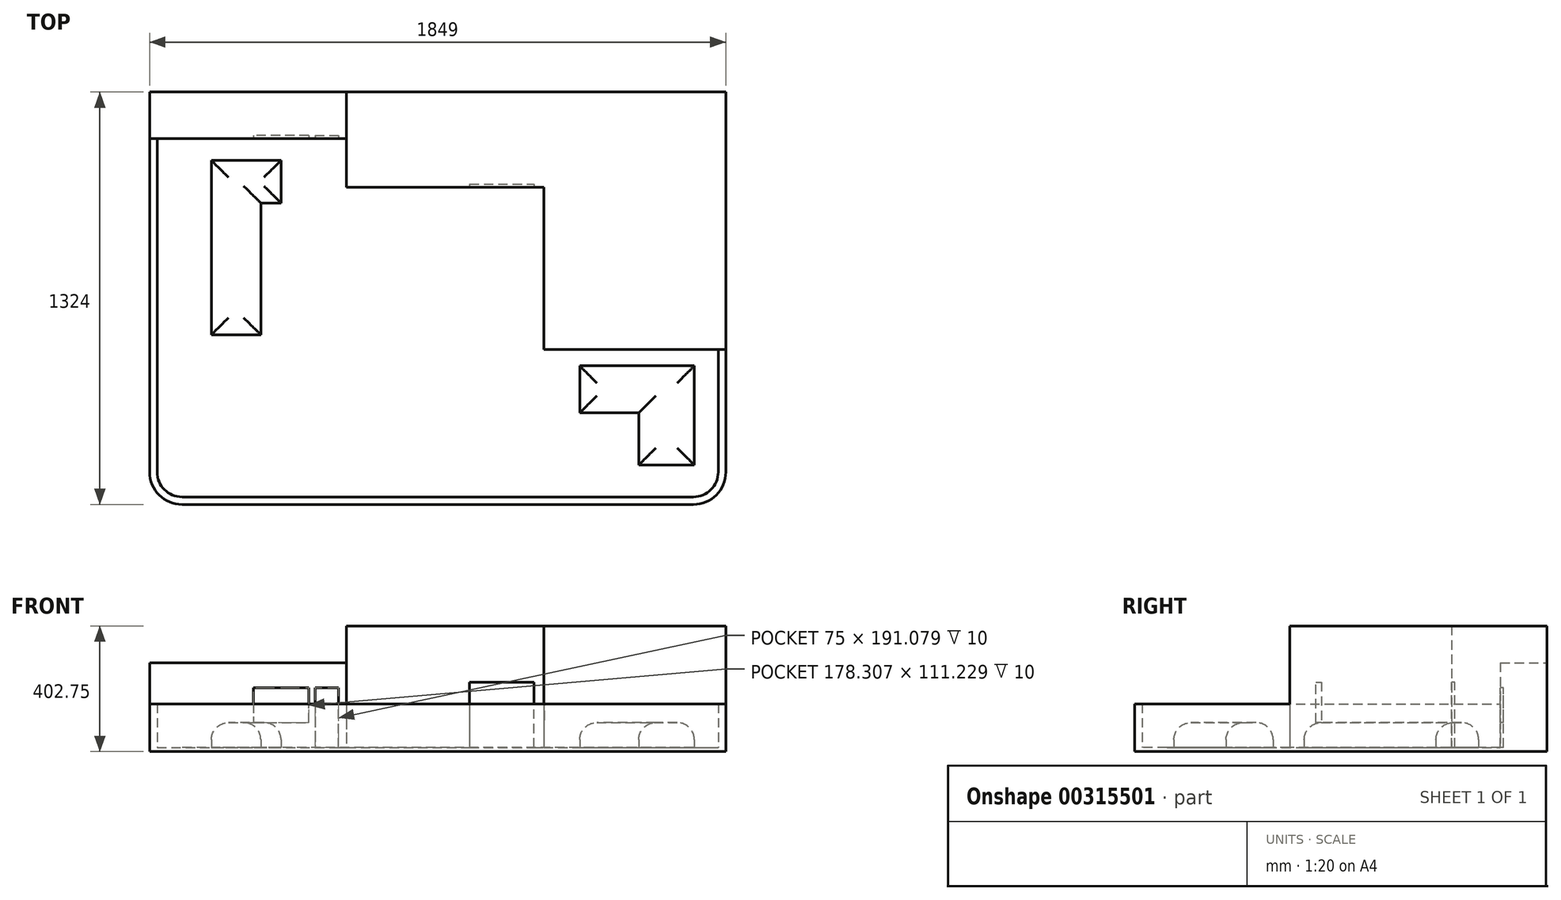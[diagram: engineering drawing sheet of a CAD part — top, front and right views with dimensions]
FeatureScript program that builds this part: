
annotation { "Feature Type Name" : "Feature", "Feature Type Description" : "" }
export const myFeature = defineFeature(function(context is Context, id is Id, definition is map)
    precondition{}
    {
        {
            var Q0;
            Q0=qCreatedBy(makeId("Top.planeOp"),FACE);
            var sketch = newSketch(context, id + "F0", { "sketchPlane" : qUnion([Q0])});
            skLineSegment(sketch, "E0", {"start": v(-3680, 5750) * mm, "end": v(-2930, 5750) * mm});
            skLineSegment(sketch, "E1", {"start": v(-2930, 5750) * mm, "end": v(-2670, 5750) * mm});
            skLineSegment(sketch, "E2", {"start": v(-2670, 5750) * mm, "end": v(-2670, 4190) * mm});
            skLineSegment(sketch, "E3", {"start": v(-2670, 4190) * mm, "end": v(1280, 4190) * mm});
            skLineSegment(sketch, "E4", {"start": v(1280, 4190) * mm, "end": v(3340, 4190) * mm});
            skLineSegment(sketch, "E5", {"start": v(3340, 4190) * mm, "end": v(3660, 4190) * mm});
            skLineSegment(sketch, "E6", {"start": v(3660, -1010) * mm, "end": v(9260, -1010) * mm});
            skLineSegment(sketch, "E7", {"start": v(9260, -1010) * mm, "end": v(9260, -4950) * mm});
            skLineSegment(sketch, "E8", {"start": v(-8750, -4950) * mm, "end": v(-8750, 5750) * mm});
            skArc(sketch, "E9", {"start": v(-8750, -4950) * mm, "mid": v(-8515.69, -5515.69) * mm, "end": v(-7950, -5750) * mm});
            skArc(sketch, "E10", {"start": v(8460, -5750) * mm, "mid": v(9025.69, -5515.69) * mm, "end": v(9260, -4950) * mm});
            skLineSegment(sketch, "E11", {"start": v(8460, -5750) * mm, "end": v(-7950, -5750) * mm});
            skLineSegment(sketch, "E12", {"start": v(3660, 4190) * mm, "end": v(3660, -1010) * mm});
            skLineSegment(sketch, "E13", {"start": v(-3680, 5750) * mm, "end": v(-8750, 5750) * mm});
            skSolve(sketch);
        }
        {
            var Q0;
            Q0=makeQuery(id+"F0.imprint","IMPRINT",FACE,{"disambiguationData":[TD([[makeQuery(id+"F0.imprint","IMPRINT",EDGE,{"derivedFrom":sQuery(id+"F0.wireOp",EDGE,"E0")}),-1.0]])]});
            extrude(context, id + "F1", {"entities" : qUnion([Q0]), "depth" : 100 * mm});
        }
        {
            var Q0;
            Q0=makeQuery(id+"F1.opExtrude","SWEPT_BODY",BODY,{"disambiguationData":[OSD([sQuery(id+"F0.wireOp",EDGE,"E0"),sQuery(id+"F0.wireOp",EDGE,"E1"),sQuery(id+"F0.wireOp",EDGE,"E2"),sQuery(id+"F0.wireOp",EDGE,"E3"),sQuery(id+"F0.wireOp",EDGE,"E4"),sQuery(id+"F0.wireOp",EDGE,"E5"),sQuery(id+"F0.wireOp",EDGE,"E6"),sQuery(id+"F0.wireOp",EDGE,"E7"),sQuery(id+"F0.wireOp",EDGE,"E8"),sQuery(id+"F0.wireOp",EDGE,"E9"),sQuery(id+"F0.wireOp",EDGE,"E10"),sQuery(id+"F0.wireOp",EDGE,"E11"),sQuery(id+"F0.wireOp",EDGE,"E12"),sQuery(id+"F0.wireOp",EDGE,"E13")])]});
            var Q1;
            Q1=qCreatedBy(makeId("Origin.pointOp"),VERTEX);
            transform(context, id + "F2", {"entities" : qUnion([Q0]), "transformType" : TransformType.SCALE_UNIFORMLY, "scale" : 1 / 10, "scalePoint" : qUnion([Q1]), "makeCopy" : false});
        }
        {
            var Q0;
            Q0=qCreatedBy(makeId("Top.planeOp"),FACE);
            var sketch = newSketch(context, id + "F3", { "sketchPlane" : qUnion([Q0])});
            skLineSegment(sketch, "E14.0", {"start": v(-899, -495) * mm, "end": v(-899, 575) * mm});
            skArc(sketch, "E15.0", {"start": v(-899, -495) * mm, "mid": v(-868.54, -568.54) * mm, "end": v(-795, -599) * mm});
            skLineSegment(sketch, "E16.0", {"start": v(846, -599) * mm, "end": v(-795, -599) * mm});
            skArc(sketch, "E17.0", {"start": v(846, -599) * mm, "mid": v(919.54, -568.54) * mm, "end": v(950, -495) * mm});
            skLineSegment(sketch, "E18.0", {"start": v(950, -101) * mm, "end": v(950, -495) * mm});
            skLineSegment(sketch, "E19.0", {"start": v(846, -575) * mm, "end": v(-795, -575) * mm});
            skArc(sketch, "E20.0", {"start": v(846, -575) * mm, "mid": v(902.57, -551.57) * mm, "end": v(926, -495) * mm});
            skLineSegment(sketch, "E21.0", {"start": v(926, -101) * mm, "end": v(926, -495) * mm});
            skLineSegment(sketch, "E22.0", {"start": v(-875, -495) * mm, "end": v(-875, 575) * mm});
            skArc(sketch, "E23.0", {"start": v(-875, -495) * mm, "mid": v(-851.57, -551.57) * mm, "end": v(-795, -575) * mm});
            skLineSegment(sketch, "E24", {"start": v(926, -101) * mm, "end": v(950, -101) * mm});
            skLineSegment(sketch, "E25", {"start": v(-875, 575) * mm, "end": v(-899, 575) * mm});
            skSolve(sketch);
        }
        {
            var Q0;
            Q0 = qSketchRegion(id + "F3", true);
            extrude(context, id + "F4", {"entities" : qUnion([Q0]), "operationType" : NewBodyOperationType.ADD, "depth" : 150 * mm});
        }
        {
            var Q0;
            Q0=qCreatedBy(makeId("Top.planeOp"),FACE);
            var sketch = newSketch(context, id + "F5", { "sketchPlane" : qUnion([Q0])});
            skLineSegment(sketch, "E26.0", {"start": v(-875, 575) * mm, "end": v(-267, 575) * mm});
            skLineSegment(sketch, "E27.0", {"start": v(-875, 575) * mm, "end": v(-899, 575) * mm});
            skLineSegment(sketch, "E28", {"start": v(-899, 575) * mm, "end": v(-899, 725) * mm});
            skLineSegment(sketch, "E29", {"start": v(-899, 725) * mm, "end": v(-267, 725) * mm});
            skLineSegment(sketch, "E30", {"start": v(-267, 725) * mm, "end": v(-267, 575) * mm});
            skSolve(sketch);
        }
        {
            var Q0;
            Q0 = qSketchRegion(id + "F5", true);
            extrude(context, id + "F6", {"entities" : qUnion([Q0]), "operationType" : NewBodyOperationType.ADD, "depth" : 282 * mm});
        }
        {
            var Q0;
            Q0=qCreatedBy(makeId("Top.planeOp"),FACE);
            var sketch = newSketch(context, id + "F7", { "sketchPlane" : qUnion([Q0])});
            skLineSegment(sketch, "E31.0", {"start": v(-267, 575) * mm, "end": v(-267, 419) * mm});
            skLineSegment(sketch, "E32.0", {"start": v(-267, 725) * mm, "end": v(-267, 575) * mm});
            skLineSegment(sketch, "E33.0", {"start": v(-267, 419) * mm, "end": v(366, 419) * mm});
            skLineSegment(sketch, "E34.0", {"start": v(366, 419) * mm, "end": v(366, -101) * mm});
            skLineSegment(sketch, "E35.0", {"start": v(366, -101) * mm, "end": v(926, -101) * mm});
            skLineSegment(sketch, "E36.0", {"start": v(926, -101) * mm, "end": v(950, -101) * mm});
            skLineSegment(sketch, "E37", {"start": v(950, -101) * mm, "end": v(950, 725) * mm});
            skLineSegment(sketch, "E38", {"start": v(950, 725) * mm, "end": v(-267, 725) * mm});
            skSolve(sketch);
        }
        {
            var Q0;
            Q0 = qSketchRegion(id + "F7", true);
            extrude(context, id + "F8", {"entities" : qUnion([Q0]), "operationType" : NewBodyOperationType.ADD, "depth" : 400 * mm});
        }
        {
            var Q0;
            Q0=makeQuery(id+"F6.opExtrude","SWEPT_FACE",FACE,{"disambiguationData":[OSD([sQuery(id+"F5.wireOp",EDGE,"E26.0"),sQuery(id+"F5.wireOp",EDGE,"E27.0")])]});
            var sketch = newSketch(context, id + "F9", { "sketchPlane" : qUnion([Q0])});
            skLineSegment(sketch, "E39.0", {"start": v(-368, 10) * mm, "end": v(-293, 10) * mm});
            skLineSegment(sketch, "E40", {"start": v(-293, 10) * mm, "end": v(-293, 201.08) * mm});
            skLineSegment(sketch, "E41", {"start": v(-293, 201.08) * mm, "end": v(-368, 201.08) * mm});
            skLineSegment(sketch, "E42", {"start": v(-368, 201.08) * mm, "end": v(-368, 10) * mm});
            skPoint(sketch, "E43.orphan", {"position": v(-267, 10) * mm});
            skPoint(sketch, "E44.orphan", {"position": v(-875, 10) * mm});
            skSolve(sketch);
        }
        {
            var Q0;
            Q0 = qSketchRegion(id + "F9", true);
            extrude(context, id + "F10", {"entities" : qUnion([Q0]), "operationType" : NewBodyOperationType.REMOVE, "oppositeDirection" : true, "depth" : 10 * mm});
        }
        {
            var Q0;
            Q0=makeQuery(id+"F6.opExtrude","SWEPT_FACE",FACE,{"disambiguationData":[OSD([sQuery(id+"F5.wireOp",EDGE,"E26.0"),sQuery(id+"F5.wireOp",EDGE,"E27.0")])]});
            var sketch = newSketch(context, id + "F11", { "sketchPlane" : qUnion([Q0])});
            skLineSegment(sketch, "E45.0", {"start": v(-368, 201.08) * mm, "end": v(-368, 10) * mm});
            skLineSegment(sketch, "E46", {"start": v(-388, 201.08) * mm, "end": v(-566.3, 201.08) * mm});
            skLineSegment(sketch, "E47", {"start": v(-566.3, 201.08) * mm, "end": v(-566.3, 89.85) * mm});
            skLineSegment(sketch, "E48", {"start": v(-566.3, 89.85) * mm, "end": v(-388, 89.85) * mm});
            skLineSegment(sketch, "E49", {"start": v(-388, 89.85) * mm, "end": v(-388, 201.08) * mm});
            skSolve(sketch);
        }
        {
            var Q0;
            Q0 = qSketchRegion(id + "F11", true);
            extrude(context, id + "F12", {"entities" : qUnion([Q0]), "operationType" : NewBodyOperationType.REMOVE, "oppositeDirection" : true, "depth" : 10 * mm});
        }
        {
            var Q0;
            Q0=makeQuery(id+"F10.boolean.opBoolean","MERGE",FACE,{"derivedFrom":[makeQuery(id+"F1.opExtrude","CAP_FACE",FACE,{"disambiguationData":[OSD([sQuery(id+"F0.wireOp",EDGE,"E0"),sQuery(id+"F0.wireOp",EDGE,"E1"),sQuery(id+"F0.wireOp",EDGE,"E2"),sQuery(id+"F0.wireOp",EDGE,"E3"),sQuery(id+"F0.wireOp",EDGE,"E4"),sQuery(id+"F0.wireOp",EDGE,"E5"),sQuery(id+"F0.wireOp",EDGE,"E6"),sQuery(id+"F0.wireOp",EDGE,"E7"),sQuery(id+"F0.wireOp",EDGE,"E8"),sQuery(id+"F0.wireOp",EDGE,"E9"),sQuery(id+"F0.wireOp",EDGE,"E10"),sQuery(id+"F0.wireOp",EDGE,"E11"),sQuery(id+"F0.wireOp",EDGE,"E12"),sQuery(id+"F0.wireOp",EDGE,"E13")])],"isStart":false}),makeQuery(id+"F10.opExtrude","SWEPT_FACE",FACE,{"disambiguationData":[OSD([sQuery(id+"F9.wireOp",EDGE,"E39.0")])]})]});
            var sketch = newSketch(context, id + "F13", { "sketchPlane" : qUnion([Q0])});
            skLineSegment(sketch, "E50.0", {"start": v(-566.3, 575) * mm, "end": v(-388, 575) * mm});
            skLineSegment(sketch, "E51", {"start": v(-477.15, 505.51) * mm, "end": v(-477.15, 368.45) * mm});
            skPoint(sketch, "E51.startSnap0", {"position": v(-477.15, 575) * mm});
            skLineSegment(sketch, "E52", {"start": v(-477.15, 368.45) * mm, "end": v(-542.33, 368.45) * mm});
            skLineSegment(sketch, "E53", {"start": v(-542.33, 368.45) * mm, "end": v(-542.33, -54.48) * mm});
            skLineSegment(sketch, "E54", {"start": v(-542.33, -54.48) * mm, "end": v(-700.93, -54.48) * mm});
            skLineSegment(sketch, "E55", {"start": v(-700.93, -54.48) * mm, "end": v(-700.93, 505.51) * mm});
            skLineSegment(sketch, "E56", {"start": v(-700.93, 505.51) * mm, "end": v(-477.15, 505.51) * mm});
            skSolve(sketch);
        }
        {
            var Q0;
            Q0 = qSketchRegion(id + "F13", true);
            var Q1;
            Q1=makeQuery(id+"F12.boolean.opBoolean","COPY",FACE,{"derivedFrom":makeQuery(id+"F12.opExtrude","SWEPT_FACE",FACE,{"disambiguationData":[OSD([sQuery(id+"F11.wireOp",EDGE,"E48")])]})});
            extrude(context, id + "F14", {"entities" : qUnion([Q0]), "operationType" : NewBodyOperationType.ADD, "endBound" : BoundingType.UP_TO_SURFACE, "endBoundEntityFace" : qUnion([Q1]), "depth" : 25 * mm});
        }
        {
            var Q0;
            Q0=makeQuery(id+"F10.boolean.opBoolean","MERGE",FACE,{"derivedFrom":[makeQuery(id+"F1.opExtrude","CAP_FACE",FACE,{"disambiguationData":[OSD([sQuery(id+"F0.wireOp",EDGE,"E0"),sQuery(id+"F0.wireOp",EDGE,"E1"),sQuery(id+"F0.wireOp",EDGE,"E2"),sQuery(id+"F0.wireOp",EDGE,"E3"),sQuery(id+"F0.wireOp",EDGE,"E4"),sQuery(id+"F0.wireOp",EDGE,"E5"),sQuery(id+"F0.wireOp",EDGE,"E6"),sQuery(id+"F0.wireOp",EDGE,"E7"),sQuery(id+"F0.wireOp",EDGE,"E8"),sQuery(id+"F0.wireOp",EDGE,"E9"),sQuery(id+"F0.wireOp",EDGE,"E10"),sQuery(id+"F0.wireOp",EDGE,"E11"),sQuery(id+"F0.wireOp",EDGE,"E12"),sQuery(id+"F0.wireOp",EDGE,"E13")])],"isStart":false}),makeQuery(id+"F10.opExtrude","SWEPT_FACE",FACE,{"disambiguationData":[OSD([sQuery(id+"F9.wireOp",EDGE,"E39.0")])]})]});
            var sketch = newSketch(context, id + "F15", { "sketchPlane" : qUnion([Q0])});
            skLineSegment(sketch, "E57", {"start": v(481.28, -153.96) * mm, "end": v(481.28, -305.16) * mm});
            skLineSegment(sketch, "E58", {"start": v(481.28, -305.16) * mm, "end": v(670.73, -305.16) * mm});
            skLineSegment(sketch, "E59", {"start": v(670.73, -305.16) * mm, "end": v(670.73, -472.75) * mm});
            skLineSegment(sketch, "E60", {"start": v(670.73, -472.75) * mm, "end": v(849.25, -472.75) * mm});
            skLineSegment(sketch, "E61", {"start": v(849.25, -472.75) * mm, "end": v(849.25, -153.96) * mm});
            skLineSegment(sketch, "E62", {"start": v(849.25, -153.96) * mm, "end": v(481.28, -153.96) * mm});
            skSolve(sketch);
        }
        {
            var Q0;
            Q0 = qSketchRegion(id + "F15", true);
            var Q1;
            Q1=makeQuery(id+"F14.opExtrude","CAP_FACE",FACE,{"disambiguationData":[OSD([sQuery(id+"F13.wireOp",EDGE,"E51"),sQuery(id+"F13.wireOp",EDGE,"E52"),sQuery(id+"F13.wireOp",EDGE,"E53"),sQuery(id+"F13.wireOp",EDGE,"E54"),sQuery(id+"F13.wireOp",EDGE,"E55"),sQuery(id+"F13.wireOp",EDGE,"E56")])],"isStart":false});
            extrude(context, id + "F16", {"entities" : qUnion([Q0]), "operationType" : NewBodyOperationType.ADD, "endBound" : BoundingType.UP_TO_SURFACE, "endBoundEntityFace" : qUnion([Q1]), "depth" : 25 * mm});
        }
        {
            var Q0;
            Q0=makeQuery(id+"F8.opExtrude","SWEPT_FACE",FACE,{"disambiguationData":[OSD([sQuery(id+"F7.wireOp",EDGE,"E33.0")])]});
            var sketch = newSketch(context, id + "F17", { "sketchPlane" : qUnion([Q0])});
            skLineSegment(sketch, "E63.0", {"start": v(-267, 10) * mm, "end": v(366, 10) * mm});
            skLineSegment(sketch, "E64", {"start": v(334, 10) * mm, "end": v(334, 220) * mm});
            skLineSegment(sketch, "E65", {"start": v(334, 220) * mm, "end": v(128, 220) * mm});
            skLineSegment(sketch, "E66", {"start": v(128, 220) * mm, "end": v(128, 10) * mm});
            skSolve(sketch);
        }
        {
            var Q0;
            Q0 = qSketchRegion(id + "F17", true);
            extrude(context, id + "F18", {"entities" : qUnion([Q0]), "operationType" : NewBodyOperationType.REMOVE, "oppositeDirection" : true, "depth" : 10 * mm});
        }
        {
            var Q0;
            Q0=makeQuery(id+"F14.opExtrude","CAP_FACE",FACE,{"disambiguationData":[OSD([sQuery(id+"F13.wireOp",EDGE,"E51"),sQuery(id+"F13.wireOp",EDGE,"E52"),sQuery(id+"F13.wireOp",EDGE,"E53"),sQuery(id+"F13.wireOp",EDGE,"E54"),sQuery(id+"F13.wireOp",EDGE,"E55"),sQuery(id+"F13.wireOp",EDGE,"E56")])],"isStart":false});
            fillet(context, id + "F19", {"entities" : qUnion([Q0]), "radius" : 55 * mm, "tangentPropagation" : true, "allowEdgeOverflow" : false});
        }
        {
            var Q0;
            Q0=makeQuery(id+"F16.opExtrude","CAP_FACE",FACE,{"disambiguationData":[OSD([sQuery(id+"F15.wireOp",EDGE,"E57"),sQuery(id+"F15.wireOp",EDGE,"E58"),sQuery(id+"F15.wireOp",EDGE,"E59"),sQuery(id+"F15.wireOp",EDGE,"E60"),sQuery(id+"F15.wireOp",EDGE,"E61"),sQuery(id+"F15.wireOp",EDGE,"E62")])],"isStart":false});
            fillet(context, id + "F20", {"entities" : qUnion([Q0]), "radius" : 55 * mm, "tangentPropagation" : true, "allowEdgeOverflow" : false});
        }
        {
            var Q0;
            Q0=makeQuery(id+"F8.boolean.opBoolean","MERGE",FACE,{"derivedFrom":[makeQuery(id+"F6.boolean.opBoolean","MERGE",FACE,{"derivedFrom":[makeQuery(id+"F4.boolean.opBoolean","MERGE",FACE,{"derivedFrom":[makeQuery(id+"F1.opExtrude","CAP_FACE",FACE,{"disambiguationData":[OSD([sQuery(id+"F0.wireOp",EDGE,"E0"),sQuery(id+"F0.wireOp",EDGE,"E1"),sQuery(id+"F0.wireOp",EDGE,"E2"),sQuery(id+"F0.wireOp",EDGE,"E3"),sQuery(id+"F0.wireOp",EDGE,"E4"),sQuery(id+"F0.wireOp",EDGE,"E5"),sQuery(id+"F0.wireOp",EDGE,"E6"),sQuery(id+"F0.wireOp",EDGE,"E7"),sQuery(id+"F0.wireOp",EDGE,"E8"),sQuery(id+"F0.wireOp",EDGE,"E9"),sQuery(id+"F0.wireOp",EDGE,"E10"),sQuery(id+"F0.wireOp",EDGE,"E11"),sQuery(id+"F0.wireOp",EDGE,"E12"),sQuery(id+"F0.wireOp",EDGE,"E13")])],"isStart":true}),makeQuery(id+"F4.opExtrude","CAP_FACE",FACE,{"disambiguationData":[OSD([sQuery(id+"F3.wireOp",EDGE,"E14.0"),sQuery(id+"F3.wireOp",EDGE,"E15.0"),sQuery(id+"F3.wireOp",EDGE,"E16.0"),sQuery(id+"F3.wireOp",EDGE,"E17.0"),sQuery(id+"F3.wireOp",EDGE,"E18.0"),sQuery(id+"F3.wireOp",EDGE,"E19.0"),sQuery(id+"F3.wireOp",EDGE,"E20.0"),sQuery(id+"F3.wireOp",EDGE,"E21.0"),sQuery(id+"F3.wireOp",EDGE,"E22.0"),sQuery(id+"F3.wireOp",EDGE,"E23.0"),sQuery(id+"F3.wireOp",EDGE,"E24"),sQuery(id+"F3.wireOp",EDGE,"E25")])],"isStart":true})]}),makeQuery(id+"F6.opExtrude","CAP_FACE",FACE,{"disambiguationData":[OSD([sQuery(id+"F5.wireOp",EDGE,"E26.0"),sQuery(id+"F5.wireOp",EDGE,"E27.0"),sQuery(id+"F5.wireOp",EDGE,"E28"),sQuery(id+"F5.wireOp",EDGE,"E29"),sQuery(id+"F5.wireOp",EDGE,"E30")])],"isStart":true})]}),makeQuery(id+"F8.opExtrude","CAP_FACE",FACE,{"disambiguationData":[OSD([sQuery(id+"F7.wireOp",EDGE,"E31.0"),sQuery(id+"F7.wireOp",EDGE,"E32.0"),sQuery(id+"F7.wireOp",EDGE,"E33.0"),sQuery(id+"F7.wireOp",EDGE,"E34.0"),sQuery(id+"F7.wireOp",EDGE,"E35.0"),sQuery(id+"F7.wireOp",EDGE,"E36.0"),sQuery(id+"F7.wireOp",EDGE,"E37"),sQuery(id+"F7.wireOp",EDGE,"E38")])],"isStart":true})]});
            extrude(context, id + "F21", {"entities" : qUnion([Q0]), "operationType" : NewBodyOperationType.ADD, "depth" : 2.75 * mm});
        }
        {
            var Q0;
            Q0=makeQuery(id+"F8.opExtrude","SWEPT_FACE",FACE,{"disambiguationData":[OSD([sQuery(id+"F7.wireOp",EDGE,"E34.0")])]});
            var sketch = newSketch(context, id + "F22", { "sketchPlane" : qUnion([Q0])});
            skLineSegment(sketch, "E67.0", {"start": v(-575, 89.85) * mm, "end": v(-575, 201.08) * mm, "construction": true});
            skLineSegment(sketch, "E68.0", {"start": v(-419, 10) * mm, "end": v(-419, 220) * mm, "construction": true});
            skLineSegment(sketch, "E69", {"start": v(-1.33, 220) * mm, "end": v(-1.33, 89.85) * mm});
            skLineSegment(sketch, "E70", {"start": v(-1.33, 89.85) * mm, "end": v(16.75, 89.85) * mm});
            skLineSegment(sketch, "E71", {"start": v(16.75, 89.85) * mm, "end": v(16.75, 220) * mm});
            skLineSegment(sketch, "E72", {"start": v(16.75, 220) * mm, "end": v(-1.33, 220) * mm});
            skSolve(sketch);
        }
        {
            var Q0;
            Q0 = qSketchRegion(id + "F22", true);
            extrude(context, id + "F23", {"entities" : qUnion([Q0]), "operationType" : NewBodyOperationType.REMOVE, "oppositeDirection" : true, "depth" : (10 / 8) * mm});
        }
    });
